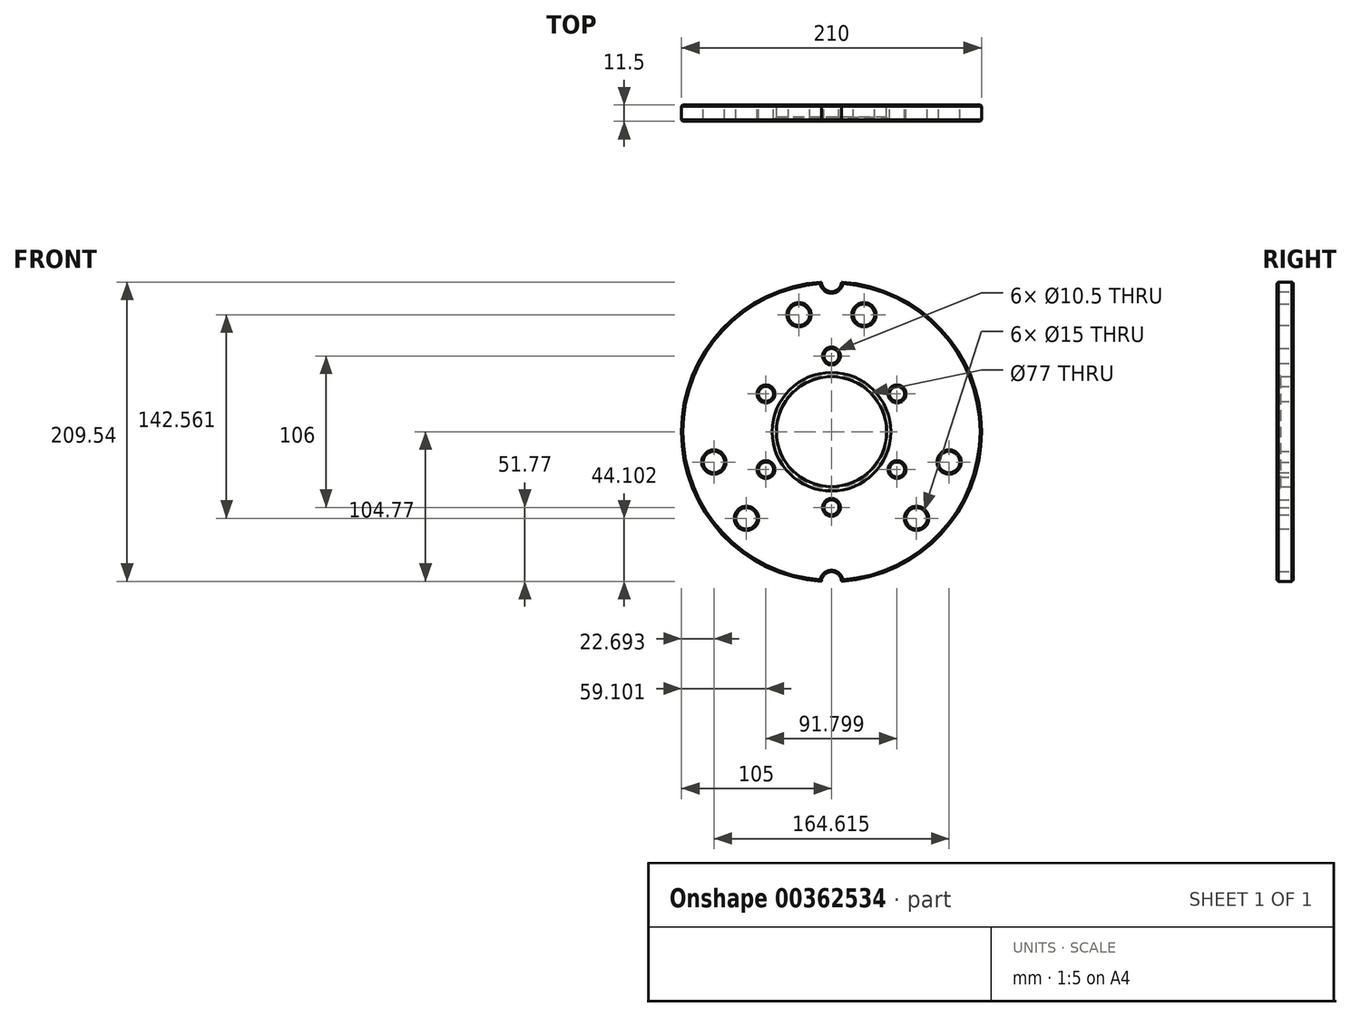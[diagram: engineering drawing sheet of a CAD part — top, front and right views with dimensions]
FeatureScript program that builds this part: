
annotation { "Feature Type Name" : "Feature", "Feature Type Description" : "" }
export const myFeature = defineFeature(function(context is Context, id is Id, definition is map)
    precondition{}
    {
        {
            var Q0;
            Q0=qCreatedBy(makeId("Front.planeOp"),FACE);
            var sketch = newSketch(context, id + "F0", { "sketchPlane" : qUnion([Q0])});
            skArc(sketch, "E0", {"start": v(-7, 104.77) * mm, "mid": v(-105, 0) * mm, "end": v(-7, -104.77) * mm});
            skCircle(sketch, "E1", {"center": v(0, 0) * mm, "radius": 38.5 * mm});
            skCircle(sketch, "E2", {"center": v(0, 53) * mm, "radius": 5.25 * mm});
            skCircle(sketch, "E3.1.0", {"center": v(-45.9, 26.5) * mm, "radius": 5.25 * mm});
            skCircle(sketch, "E3.2.0", {"center": v(-45.9, -26.5) * mm, "radius": 5.25 * mm});
            skCircle(sketch, "E3.3.0", {"center": v(0, -53) * mm, "radius": 5.25 * mm});
            skCircle(sketch, "E3.4.0", {"center": v(45.9, -26.5) * mm, "radius": 5.25 * mm});
            skCircle(sketch, "E3.5.0", {"center": v(45.9, 26.5) * mm, "radius": 5.25 * mm});
            skCircle(sketch, "E4", {"center": v(-22.77, 81.9) * mm, "radius": 7.5 * mm});
            skCircle(sketch, "E5.1.0", {"center": v(-59.53, -60.67) * mm, "radius": 7.5 * mm});
            skCircle(sketch, "E5.2.0", {"center": v(82.3, -21.22) * mm, "radius": 7.5 * mm});
            skCircle(sketch, "E6", {"center": v(22.77, 81.9) * mm, "radius": 7.5 * mm});
            skCircle(sketch, "E7.1.0", {"center": v(-82.3, -21.22) * mm, "radius": 7.5 * mm});
            skCircle(sketch, "E7.2.0", {"center": v(59.53, -60.67) * mm, "radius": 7.5 * mm});
            skArc(sketch, "E8", {"start": v(-7, 104.77) * mm, "mid": v(0, 98) * mm, "end": v(7, 104.77) * mm});
            skArc(sketch, "E9", {"start": v(7, -104.77) * mm, "mid": v(0, -98) * mm, "end": v(-7, -104.77) * mm});
            skArc(sketch, "E10.trimOffspring", {"start": v(7, -104.77) * mm, "mid": v(105, 0) * mm, "end": v(7, 104.77) * mm});
            skSolve(sketch);
        }
        {
            var Q0;
            Q0=makeQuery(id+"F0.imprint","IMPRINT",FACE,{"disambiguationData":[TD([[makeQuery(id+"F0.imprint","IMPRINT",EDGE,{"derivedFrom":sQuery(id+"F0.wireOp",EDGE,"E0")}),1.0]])]});
            extrude(context, id + "F1", {"entities" : qUnion([Q0]), "depth" : 11.5 * mm});
        }
        {
            var Q0;
            Q0=makeQuery(id+"F1.opExtrude","CAP_EDGE",EDGE,{"disambiguationData":[OSD([sQuery(id+"F0.wireOp",EDGE,"E8")])],"isStart":false});
            var Q1;
            Q1=makeQuery(id+"F1.opExtrude","CAP_EDGE",EDGE,{"disambiguationData":[OSD([sQuery(id+"F0.wireOp",EDGE,"E10.trimOffspring")])],"isStart":false});
            var Q2;
            Q2=makeQuery(id+"F1.opExtrude","CAP_EDGE",EDGE,{"disambiguationData":[OSD([sQuery(id+"F0.wireOp",EDGE,"E0")])],"isStart":false});
            var Q3;
            Q3=makeQuery(id+"F1.opExtrude","CAP_EDGE",EDGE,{"disambiguationData":[OSD([sQuery(id+"F0.wireOp",EDGE,"E4")])],"isStart":false});
            var Q4;
            Q4=makeQuery(id+"F1.opExtrude","CAP_EDGE",EDGE,{"disambiguationData":[OSD([sQuery(id+"F0.wireOp",EDGE,"E6")])],"isStart":false});
            var Q5;
            Q5=makeQuery(id+"F1.opExtrude","CAP_EDGE",EDGE,{"disambiguationData":[OSD([sQuery(id+"F0.wireOp",EDGE,"E2")])],"isStart":false});
            var Q6;
            Q6=makeQuery(id+"F1.opExtrude","CAP_EDGE",EDGE,{"disambiguationData":[OSD([sQuery(id+"F0.wireOp",EDGE,"E3.5.0")])],"isStart":false});
            var Q7;
            Q7=makeQuery(id+"F1.opExtrude","CAP_EDGE",EDGE,{"disambiguationData":[OSD([sQuery(id+"F0.wireOp",EDGE,"E3.4.0")])],"isStart":false});
            var Q8;
            Q8=makeQuery(id+"F1.opExtrude","CAP_EDGE",EDGE,{"disambiguationData":[OSD([sQuery(id+"F0.wireOp",EDGE,"E5.2.0")])],"isStart":false});
            var Q9;
            Q9=makeQuery(id+"F1.opExtrude","CAP_EDGE",EDGE,{"disambiguationData":[OSD([sQuery(id+"F0.wireOp",EDGE,"E7.2.0")])],"isStart":false});
            var Q10;
            Q10=makeQuery(id+"F1.opExtrude","CAP_EDGE",EDGE,{"disambiguationData":[OSD([sQuery(id+"F0.wireOp",EDGE,"E3.3.0")])],"isStart":false});
            var Q11;
            Q11=makeQuery(id+"F1.opExtrude","CAP_EDGE",EDGE,{"disambiguationData":[OSD([sQuery(id+"F0.wireOp",EDGE,"E5.1.0")])],"isStart":false});
            var Q12;
            Q12=makeQuery(id+"F1.opExtrude","CAP_EDGE",EDGE,{"disambiguationData":[OSD([sQuery(id+"F0.wireOp",EDGE,"E7.1.0")])],"isStart":false});
            var Q13;
            Q13=makeQuery(id+"F1.opExtrude","CAP_EDGE",EDGE,{"disambiguationData":[OSD([sQuery(id+"F0.wireOp",EDGE,"E3.2.0")])],"isStart":false});
            var Q14;
            Q14=makeQuery(id+"F1.opExtrude","CAP_EDGE",EDGE,{"disambiguationData":[OSD([sQuery(id+"F0.wireOp",EDGE,"E3.1.0")])],"isStart":false});
            var Q15;
            Q15=makeQuery(id+"F1.opExtrude","CAP_EDGE",EDGE,{"disambiguationData":[OSD([sQuery(id+"F0.wireOp",EDGE,"E9")])],"isStart":false});
            chamfer(context, id + "F2", {"entities" : qUnion([Q0, Q1, Q2, Q3, Q4, Q5, Q6, Q7, Q8, Q9, Q10, Q11, Q12, Q13, Q14, Q15]), "chamferType" : ChamferType.OFFSET_ANGLE, "width" : 1 * mm, "oppositeDirection" : false, "angle" : 45 * degree, "tangentPropagation" : true});
        }
        {
            var Q0;
            Q0=makeQuery(id+"F1.opExtrude","CAP_EDGE",EDGE,{"disambiguationData":[OSD([sQuery(id+"F0.wireOp",EDGE,"E1")])],"isStart":false});
            chamfer(context, id + "F3", {"entities" : qUnion([Q0]), "chamferType" : ChamferType.OFFSET_ANGLE, "width" : 3 * mm, "oppositeDirection" : false, "angle" : 45 * degree, "tangentPropagation" : true});
        }
        {
            var Q0;
            Q0=makeQuery(id+"F1.opExtrude","CAP_EDGE",EDGE,{"disambiguationData":[OSD([sQuery(id+"F0.wireOp",EDGE,"E10.trimOffspring")])],"isStart":true});
            var Q1;
            Q1=makeQuery(id+"F1.opExtrude","CAP_EDGE",EDGE,{"disambiguationData":[OSD([sQuery(id+"F0.wireOp",EDGE,"E0")])],"isStart":true});
            var Q2;
            Q2=makeQuery(id+"F1.opExtrude","CAP_EDGE",EDGE,{"disambiguationData":[OSD([sQuery(id+"F0.wireOp",EDGE,"E8")])],"isStart":true});
            var Q3;
            Q3=makeQuery(id+"F1.opExtrude","CAP_EDGE",EDGE,{"disambiguationData":[OSD([sQuery(id+"F0.wireOp",EDGE,"E6")])],"isStart":true});
            var Q4;
            Q4=makeQuery(id+"F1.opExtrude","CAP_EDGE",EDGE,{"disambiguationData":[OSD([sQuery(id+"F0.wireOp",EDGE,"E4")])],"isStart":true});
            var Q5;
            Q5=makeQuery(id+"F1.opExtrude","CAP_EDGE",EDGE,{"disambiguationData":[OSD([sQuery(id+"F0.wireOp",EDGE,"E3.1.0")])],"isStart":true});
            var Q6;
            Q6=makeQuery(id+"F1.opExtrude","CAP_EDGE",EDGE,{"disambiguationData":[OSD([sQuery(id+"F0.wireOp",EDGE,"E5.2.0")])],"isStart":true});
            var Q7;
            Q7=makeQuery(id+"F1.opExtrude","CAP_EDGE",EDGE,{"disambiguationData":[OSD([sQuery(id+"F0.wireOp",EDGE,"E3.5.0")])],"isStart":true});
            var Q8;
            Q8=makeQuery(id+"F1.opExtrude","CAP_EDGE",EDGE,{"disambiguationData":[OSD([sQuery(id+"F0.wireOp",EDGE,"E3.4.0")])],"isStart":true});
            var Q9;
            Q9=makeQuery(id+"F1.opExtrude","CAP_EDGE",EDGE,{"disambiguationData":[OSD([sQuery(id+"F0.wireOp",EDGE,"E3.3.0")])],"isStart":true});
            var Q10;
            Q10=makeQuery(id+"F1.opExtrude","CAP_EDGE",EDGE,{"disambiguationData":[OSD([sQuery(id+"F0.wireOp",EDGE,"E3.2.0")])],"isStart":true});
            var Q11;
            Q11=makeQuery(id+"F1.opExtrude","CAP_EDGE",EDGE,{"disambiguationData":[OSD([sQuery(id+"F0.wireOp",EDGE,"E7.1.0")])],"isStart":true});
            var Q12;
            Q12=makeQuery(id+"F1.opExtrude","CAP_EDGE",EDGE,{"disambiguationData":[OSD([sQuery(id+"F0.wireOp",EDGE,"E9")])],"isStart":true});
            var Q13;
            Q13=makeQuery(id+"F1.opExtrude","CAP_EDGE",EDGE,{"disambiguationData":[OSD([sQuery(id+"F0.wireOp",EDGE,"E5.1.0")])],"isStart":true});
            var Q14;
            Q14=makeQuery(id+"F1.opExtrude","CAP_EDGE",EDGE,{"disambiguationData":[OSD([sQuery(id+"F0.wireOp",EDGE,"E7.2.0")])],"isStart":true});
            var Q15;
            Q15=makeQuery(id+"F1.opExtrude","CAP_EDGE",EDGE,{"disambiguationData":[OSD([sQuery(id+"F0.wireOp",EDGE,"E2")])],"isStart":true});
            var Q16;
            Q16=makeQuery(id+"F1.opExtrude","CAP_EDGE",EDGE,{"disambiguationData":[OSD([sQuery(id+"F0.wireOp",EDGE,"E1")])],"isStart":true});
            chamfer(context, id + "F4", {"entities" : qUnion([Q0, Q1, Q2, Q3, Q4, Q5, Q6, Q7, Q8, Q9, Q10, Q11, Q12, Q13, Q14, Q15, Q16]), "chamferType" : ChamferType.OFFSET_ANGLE, "width" : 1 * mm, "oppositeDirection" : true, "angle" : 45 * degree, "tangentPropagation" : true});
        }
    });
